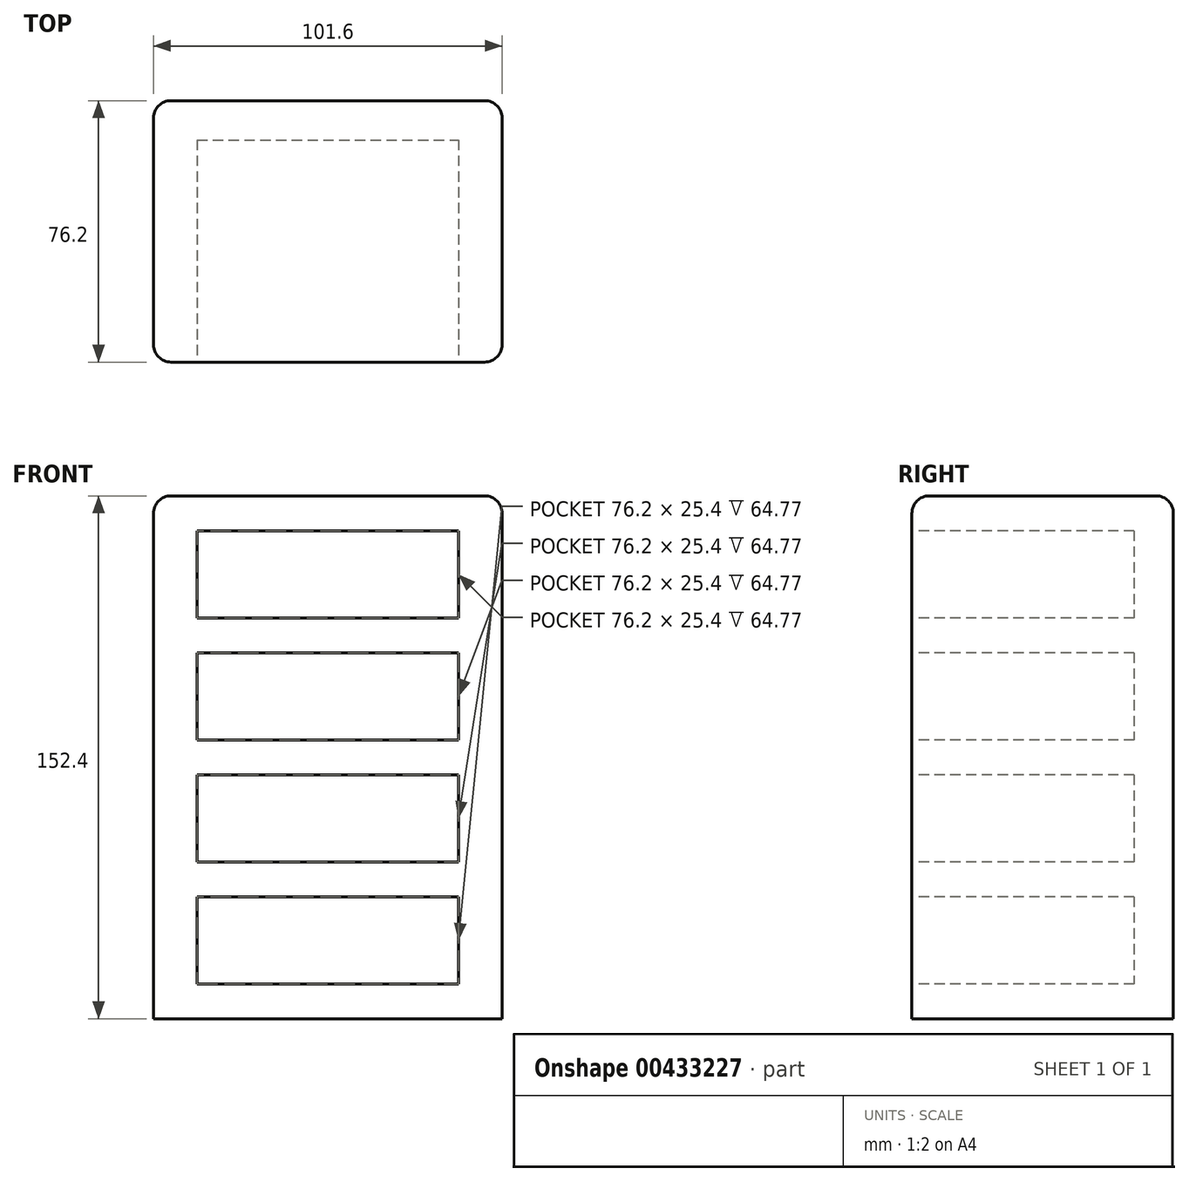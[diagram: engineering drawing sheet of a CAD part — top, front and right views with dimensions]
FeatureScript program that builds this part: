
annotation { "Feature Type Name" : "Feature", "Feature Type Description" : "" }
export const myFeature = defineFeature(function(context is Context, id is Id, definition is map)
    precondition{}
    {
        {
            var Q0;
            Q0=qCreatedBy(makeId("Top.planeOp"),FACE);
            var sketch = newSketch(context, id + "F0", { "sketchPlane" : qUnion([Q0])});
            skLineSegment(sketch, "E0.bottom", {"start": v(0, 0) * mm, "end": v(-101.6, 0) * mm});
            skLineSegment(sketch, "E0.top", {"start": v(0, 76.2) * mm, "end": v(-101.6, 76.2) * mm});
            skLineSegment(sketch, "E0.left", {"start": v(0, 0) * mm, "end": v(0, 76.2) * mm});
            skLineSegment(sketch, "E0.right", {"start": v(-101.6, 0) * mm, "end": v(-101.6, 76.2) * mm});
            skSolve(sketch);
        }
        {
            var Q0;
            Q0=makeQuery(id+"F0.imprint","IMPRINT",FACE,{"disambiguationData":[TD([[makeQuery(id+"F0.imprint","IMPRINT",EDGE,{"derivedFrom":sQuery(id+"F0.wireOp",EDGE,"E0.bottom")}),-1.0]])]});
            extrude(context, id + "F1", {"entities" : qUnion([Q0]), "depth" : 152.4 * mm});
        }
        {
            var Q0;
            Q0=makeQuery(id+"F1.opExtrude","SWEPT_FACE",FACE,{"disambiguationData":[OSD([sQuery(id+"F0.wireOp",EDGE,"E0.bottom")])]});
            var sketch = newSketch(context, id + "F2", { "sketchPlane" : qUnion([Q0])});
            skLineSegment(sketch, "E1.bottom", {"start": v(-88.9, 142.24) * mm, "end": v(-12.7, 142.24) * mm});
            skLineSegment(sketch, "E1.top", {"start": v(-88.9, 116.84) * mm, "end": v(-12.7, 116.84) * mm});
            skLineSegment(sketch, "E1.left", {"start": v(-88.9, 142.24) * mm, "end": v(-88.9, 116.84) * mm});
            skLineSegment(sketch, "E1.right", {"start": v(-12.7, 142.24) * mm, "end": v(-12.7, 116.84) * mm});
            skLineSegment(sketch, "E2.0.1.0", {"start": v(-88.9, 106.68) * mm, "end": v(-88.9, 81.28) * mm});
            skLineSegment(sketch, "E2.0.1.1", {"start": v(-88.9, 106.68) * mm, "end": v(-12.7, 106.68) * mm});
            skLineSegment(sketch, "E2.0.1.2", {"start": v(-12.7, 106.68) * mm, "end": v(-12.7, 81.28) * mm});
            skLineSegment(sketch, "E2.0.1.3", {"start": v(-88.9, 81.28) * mm, "end": v(-12.7, 81.28) * mm});
            skLineSegment(sketch, "E2.0.2.0", {"start": v(-88.9, 71.12) * mm, "end": v(-88.9, 45.72) * mm});
            skLineSegment(sketch, "E2.0.2.1", {"start": v(-88.9, 71.12) * mm, "end": v(-12.7, 71.12) * mm});
            skLineSegment(sketch, "E2.0.2.2", {"start": v(-12.7, 71.12) * mm, "end": v(-12.7, 45.72) * mm});
            skLineSegment(sketch, "E2.0.2.3", {"start": v(-88.9, 45.72) * mm, "end": v(-12.7, 45.72) * mm});
            skLineSegment(sketch, "E2.0.3.0", {"start": v(-88.9, 35.56) * mm, "end": v(-88.9, 10.16) * mm});
            skLineSegment(sketch, "E2.0.3.1", {"start": v(-88.9, 35.56) * mm, "end": v(-12.7, 35.56) * mm});
            skLineSegment(sketch, "E2.0.3.2", {"start": v(-12.7, 35.56) * mm, "end": v(-12.7, 10.16) * mm});
            skLineSegment(sketch, "E2.0.3.3", {"start": v(-88.9, 10.16) * mm, "end": v(-12.7, 10.16) * mm});
            skLineSegment(sketch, "E2.direction1", {"start": v(-88.9, 116.84) * mm, "end": v(-74.93, 116.84) * mm, "construction": true});
            skLineSegment(sketch, "E2.direction2", {"start": v(-88.9, 116.84) * mm, "end": v(-88.9, 81.28) * mm, "construction": true});
            skSolve(sketch);
        }
        {
            var Q0;
            Q0=makeQuery(id+"F2.imprint","IMPRINT",FACE,{"disambiguationData":[TD([[makeQuery(id+"F2.imprint","IMPRINT",EDGE,{"derivedFrom":sQuery(id+"F2.wireOp",EDGE,"E1.bottom")}),-1.0]])]});
            var Q1;
            Q1=makeQuery(id+"F2.imprint","IMPRINT",FACE,{"disambiguationData":[TD([[makeQuery(id+"F2.imprint","IMPRINT",EDGE,{"derivedFrom":sQuery(id+"F2.wireOp",EDGE,"E2.0.1.0")}),1.0]])]});
            var Q2;
            Q2=makeQuery(id+"F2.imprint","IMPRINT",FACE,{"disambiguationData":[TD([[makeQuery(id+"F2.imprint","IMPRINT",EDGE,{"derivedFrom":sQuery(id+"F2.wireOp",EDGE,"E2.0.2.0")}),1.0]])]});
            var Q3;
            Q3=makeQuery(id+"F2.imprint","IMPRINT",FACE,{"disambiguationData":[TD([[makeQuery(id+"F2.imprint","IMPRINT",EDGE,{"derivedFrom":sQuery(id+"F2.wireOp",EDGE,"E2.0.3.0")}),1.0]])]});
            extrude(context, id + "F3", {"entities" : qUnion([Q0, Q1, Q2, Q3]), "operationType" : NewBodyOperationType.REMOVE, "oppositeDirection" : true, "depth" : 64.77 * mm});
        }
        {
            var Q0;
            Q0=makeQuery(id+"F1.opExtrude","CAP_EDGE",EDGE,{"disambiguationData":[OSD([sQuery(id+"F0.wireOp",EDGE,"E0.bottom")])],"isStart":false});
            var Q1;
            Q1=makeQuery(id+"F1.opExtrude","CAP_EDGE",EDGE,{"disambiguationData":[OSD([sQuery(id+"F0.wireOp",EDGE,"E0.right")])],"isStart":false});
            fillet(context, id + "F4", {"entities" : qUnion([Q0, Q1]), "radius" : 5.08 * mm, "tangentPropagation" : true, "allowEdgeOverflow" : false});
        }
        {
            var Q0;
            Q0=makeQuery(id+"F1.opExtrude","CAP_EDGE",EDGE,{"disambiguationData":[OSD([sQuery(id+"F0.wireOp",EDGE,"E0.left")])],"isStart":false});
            var Q1;
            Q1=makeQuery(id+"F1.opExtrude","CAP_EDGE",EDGE,{"disambiguationData":[OSD([sQuery(id+"F0.wireOp",EDGE,"E0.top")])],"isStart":false});
            fillet(context, id + "F5", {"entities" : qUnion([Q0, Q1]), "radius" : 5.08 * mm, "tangentPropagation" : true, "allowEdgeOverflow" : false});
        }
        {
            var Q0;
            Q0=makeQuery(id+"F1.opExtrude","SWEPT_EDGE",EDGE,{"disambiguationData":[OSD([sQuery(id+"F0.wireOp",EDGE,"E0.top"),sQuery(id+"F0.wireOp",EDGE,"E0.left")])]});
            var Q1;
            Q1=makeQuery(id+"F1.opExtrude","SWEPT_EDGE",EDGE,{"disambiguationData":[OSD([sQuery(id+"F0.wireOp",EDGE,"E0.bottom"),sQuery(id+"F0.wireOp",EDGE,"E0.right")])]});
            fillet(context, id + "F6", {"entities" : qUnion([Q0, Q1]), "radius" : 5.08 * mm, "tangentPropagation" : true, "allowEdgeOverflow" : false});
        }
    });
